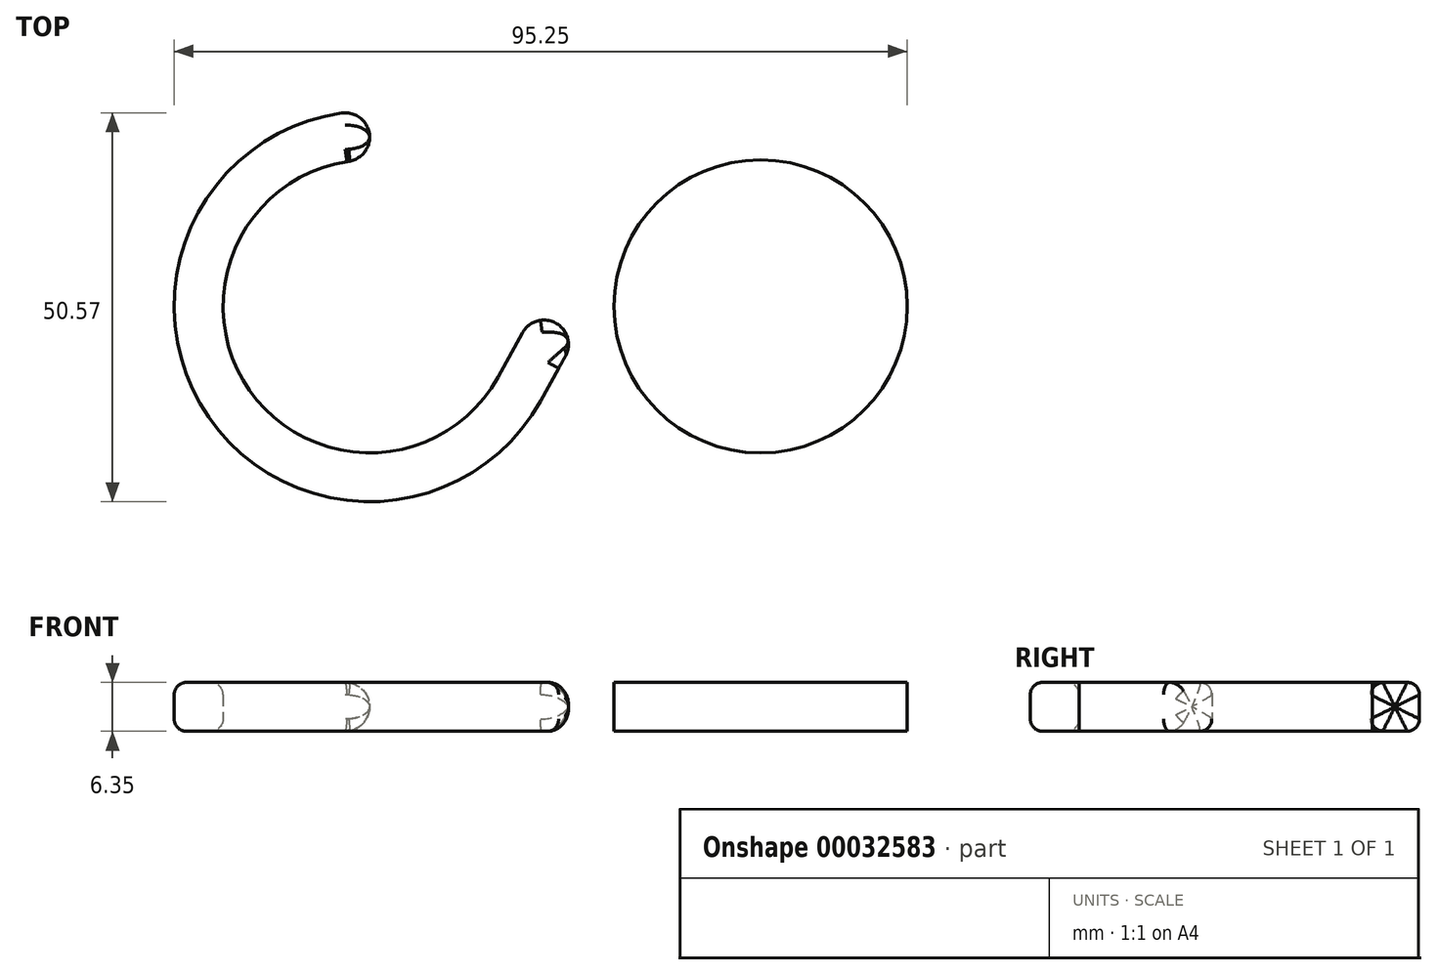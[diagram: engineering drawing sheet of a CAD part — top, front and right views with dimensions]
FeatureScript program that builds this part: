
annotation { "Feature Type Name" : "Feature", "Feature Type Description" : "" }
export const myFeature = defineFeature(function(context is Context, id is Id, definition is map)
    precondition{}
    {
        {
            var Q0;
            Q0=qCreatedBy(makeId("Top.planeOp"),FACE);
            var sketch = newSketch(context, id + "F1", { "sketchPlane" : qUnion([Q0])});
            skCircle(sketch, "E0", {"center": v(-25.4, 0) * mm, "radius": 19.05 * mm});
            skLineSegment(sketch, "E1", {"start": v(0, 21.36) * mm, "end": v(0, -26.95) * mm, "construction": true});
            skCircle(sketch, "E2.MirrorC", {"center": v(25.4, 0) * mm, "radius": 19.05 * mm});
            skCircle(sketch, "E3", {"center": v(-25.4, 0) * mm, "radius": 25.4 * mm});
            skCircle(sketch, "E4.MirrorC", {"center": v(25.4, 0) * mm, "radius": 25.4 * mm});
            skLineSegment(sketch, "E5", {"start": v(-8.73, -9.22) * mm, "end": v(3.17, 12.3) * mm});
            skLineSegment(sketch, "E6", {"start": v(25.4, 0) * mm, "end": v(3.17, 12.3) * mm, "construction": true});
            skLineSegment(sketch, "E7", {"start": v(-25.4, 0) * mm, "end": v(-3.17, -12.3) * mm, "construction": true});
            skLineSegment(sketch, "E8", {"start": v(8.73, 9.22) * mm, "end": v(-3.17, -12.3) * mm});
            skLineSegment(sketch, "E9", {"start": v(25.4, 0) * mm, "end": v(25.4, -25.4) * mm});
            skLineSegment(sketch, "E10", {"start": v(-25.4, 0) * mm, "end": v(-25.4, 25.4) * mm});
            skSolve(sketch);
        }
        {
            var Q0;
            {var subQ0=sQuery(id+"F1.wireOp",EDGE,"E8");var subQ3=sQuery(id+"F1.wireOp",EDGE,"E3");var subQ4=makeQuery(id+"F1.imprint","INTERSECT",VERTEX,{"derivedFrom":[subQ3,subQ0]});Q0=makeQuery(id+"F1.imprint","IMPRINT",FACE,{"disambiguationData":[TD([[makeQuery(id+"F1.imprint","IMPRINT",EDGE,{"disambiguationData":[TD([[subQ4,-1.0]])],"derivedFrom":subQ3}),-1.0]])]});}
            var Q1;
            {var subQ0=sQuery(id+"F1.wireOp",EDGE,"E2.MirrorC");var subQ3=sQuery(id+"F1.wireOp",EDGE,"E8");var subQ4=makeQuery(id+"F1.imprint","INTERSECT",VERTEX,{"derivedFrom":[subQ0,subQ3]});Q1=makeQuery(id+"F1.imprint","IMPRINT",FACE,{"disambiguationData":[TD([[makeQuery(id+"F1.imprint","IMPRINT",EDGE,{"disambiguationData":[TD([[subQ4,-1.0]])],"derivedFrom":subQ0}),1.0]])]});}
            var Q2;
            {var subQ1=sQuery(id+"F1.wireOp",EDGE,"E0");var subQ5=sQuery(id+"F1.wireOp",EDGE,"E5");var subQ6=makeQuery(id+"F1.imprint","INTERSECT",VERTEX,{"derivedFrom":[subQ1,subQ5]});Q2=makeQuery(id+"F1.imprint","IMPRINT",FACE,{"disambiguationData":[TD([[makeQuery(id+"F1.imprint","IMPRINT",EDGE,{"disambiguationData":[TD([[subQ6,1.0]])],"derivedFrom":subQ1}),-1.0]])]});}
            var Q3;
            {var subQ0=sQuery(id+"F1.wireOp",EDGE,"E5");var subQ1=sQuery(id+"F1.wireOp",EDGE,"E3");var subQ2=makeQuery(id+"F1.imprint","INTERSECT",VERTEX,{"derivedFrom":[subQ1,subQ0]});Q3=makeQuery(id+"F1.imprint","IMPRINT",FACE,{"disambiguationData":[TD([[makeQuery(id+"F1.imprint","IMPRINT",EDGE,{"disambiguationData":[TD([[subQ2,1.0]])],"derivedFrom":subQ1}),-1.0]])]});}
            extrude(context, id + "F2", {"entities" : qUnion([Q0, Q1, Q2, Q3]), "depth" : 6.35 * mm});
        }
        {
            var Q0;
            Q0=makeQuery(id+"F2.opExtrude","CAP_EDGE",EDGE,{"disambiguationData":[OSD([sQuery(id+"F1.wireOp",EDGE,"E0")])],"isStart":false});
            var Q1;
            Q1=makeQuery(id+"F2.opExtrude","CAP_EDGE",EDGE,{"disambiguationData":[OSD([sQuery(id+"F1.wireOp",EDGE,"E3")])],"isStart":false});
            var Q2;
            Q2=makeQuery(id+"F2.opExtrude","CAP_EDGE",EDGE,{"disambiguationData":[OSD([sQuery(id+"F1.wireOp",EDGE,"E3")])],"isStart":true});
            var Q3;
            Q3=makeQuery(id+"F2.opExtrude","CAP_EDGE",EDGE,{"disambiguationData":[OSD([sQuery(id+"F1.wireOp",EDGE,"E0")])],"isStart":true});
            fillet(context, id + "F0", {"entities" : qUnion([Q0, Q1, Q2, Q3]), "radius" : 1.59 * mm, "tangentPropagation" : true, "allowEdgeOverflow" : false});
        }
        {
            var Q0;
            Q0=makeQuery(id+"F2.opExtrude","SWEPT_EDGE",EDGE,{"disambiguationData":[OSD([sQuery(id+"F1.wireOp",EDGE,"E4.MirrorC"),sQuery(id+"F1.wireOp",EDGE,"E9")])]});
            var Q1;
            Q1=makeQuery(id+"F2.opExtrude","SWEPT_EDGE",EDGE,{"disambiguationData":[OSD([sQuery(id+"F1.wireOp",EDGE,"E0"),sQuery(id+"F1.wireOp",EDGE,"E10")])]});
            fillet(context, id + "F3", {"entities" : qUnion([Q0, Q1]), "radius" : 3.17 * mm, "tangentPropagation" : true, "allowEdgeOverflow" : false});
        }
    });
